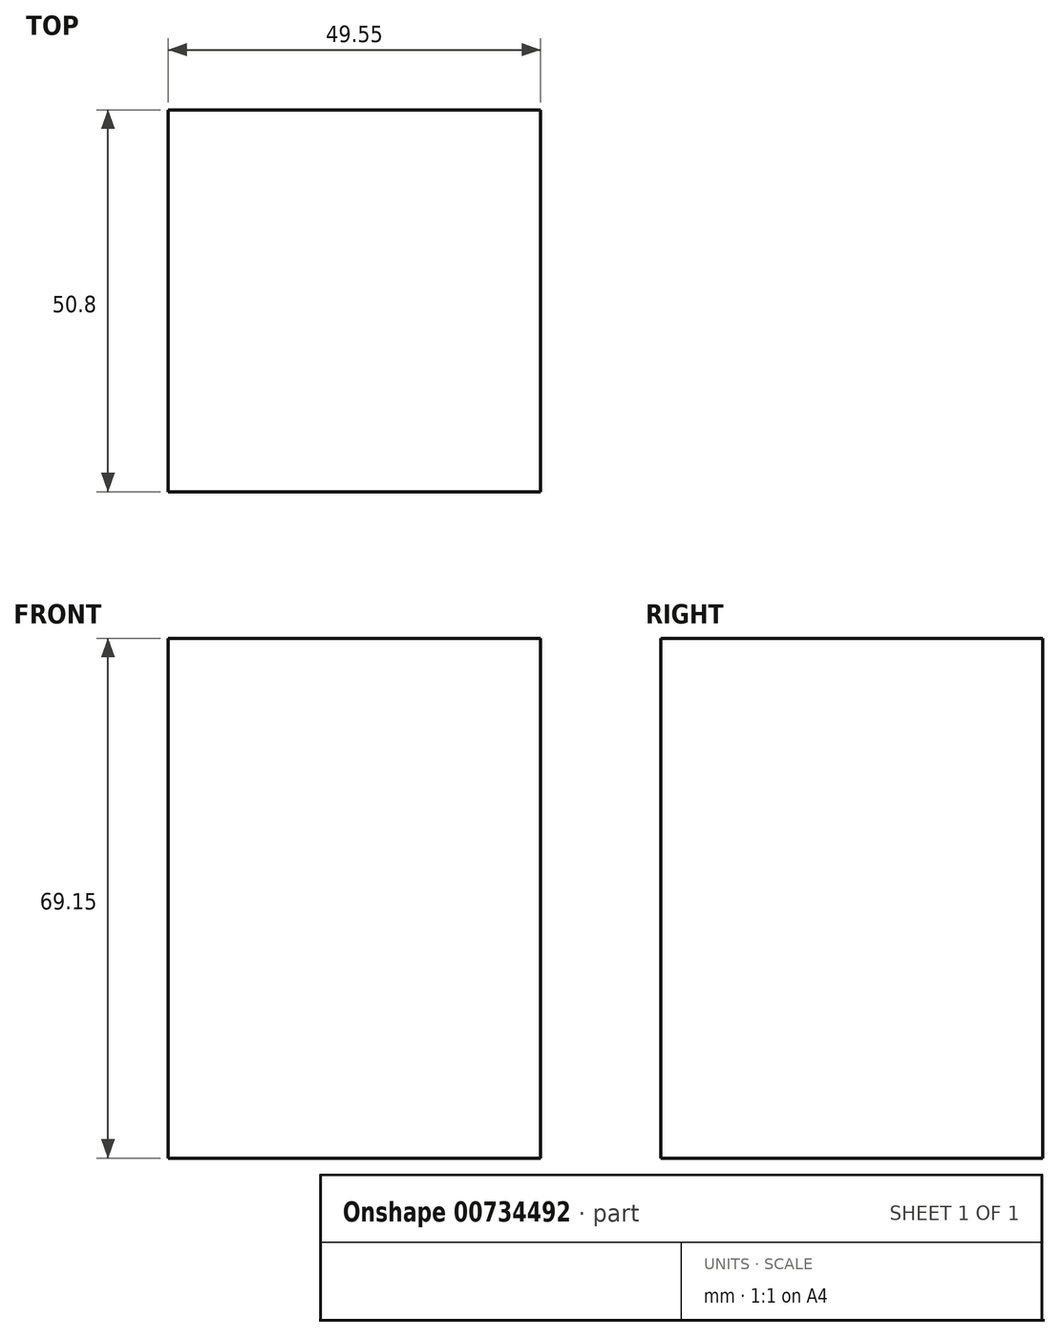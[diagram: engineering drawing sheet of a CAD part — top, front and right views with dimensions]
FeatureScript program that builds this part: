
annotation { "Feature Type Name" : "Feature", "Feature Type Description" : "" }
export const myFeature = defineFeature(function(context is Context, id is Id, definition is map)
    precondition{}
    {
        {
            var Q0;
            Q0=qCreatedBy(makeId("Front.planeOp"),FACE);
            var sketch = newSketch(context, id + "F0", { "sketchPlane" : qUnion([Q0])});
            skLineSegment(sketch, "E0.bottom", {"start": v(-61.12, 41.85) * mm, "end": v(-11.57, 41.85) * mm});
            skLineSegment(sketch, "E0.top", {"start": v(-61.12, -27.3) * mm, "end": v(-11.57, -27.3) * mm});
            skLineSegment(sketch, "E0.left", {"start": v(-61.12, 41.85) * mm, "end": v(-61.12, -27.3) * mm});
            skLineSegment(sketch, "E0.right", {"start": v(-11.57, 41.85) * mm, "end": v(-11.57, -27.3) * mm});
            skSolve(sketch);
        }
        {
            var Q0;
            Q0 = qSketchRegion(id + "F0", true);
            extrude(context, id + "F1", {"entities" : qUnion([Q0]), "depth" : 50.8 * mm, "offsetDistance" : 25.4 * mm});
        }
    });
